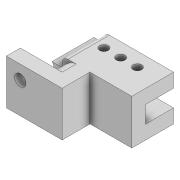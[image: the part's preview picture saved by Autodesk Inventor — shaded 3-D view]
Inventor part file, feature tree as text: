
AUTODESK INVENTOR PART (.ipt)
format: ipt  version: 2022 (Build 260153000, 153)  size: 222,208 bytes
history: native  units: mm
features: extrude x9, sketch x6, projected_geometry x6, pattern_linear x2, fillet x2, plane x1, mirror x1
ambient origin geometry x8: Origin, YZ Plane, XZ Plane, XY Plane, X Axis, Y Axis, Z Axis, Center Point
bodies: Solid1 (feature_tree)
feature tree (27):
  sketch  "Sketch2"  dims[d0=3.1mm d1=10.0mm]
  extrude  "Extrusion1"  Depth=10.0mm
  extrude  "Extrusion2"  Depth=30.0mm
  pattern_linear  "Rectangular Pattern1"  Count1=3 Spacing1=6.0mm
  pattern_linear  "Rectangular Pattern2"  Count1=2 Spacing1=11.1mm
  sketch  "Sketch3"  dims[d2=5.0mm d3=30.0mm]
  extrude  "Extrusion3"  Depth=2.0mm TaperAngle=0.0deg
  extrude  "Extrusion4"  Depth=10.0mm TaperAngle=0.0deg
  extrude  "Extrusion5"  Depth=2.0mm
  extrude  "Extrusion8"  Depth=5.0mm
  plane  "Work Plane2"
  mirror  "Mirror2"
  extrude  "Extrusion9"  Depth=5.0mm
  extrude  "Extrusion10"  Depth=5.0mm
  fillet  "Fillet1"  Radius=5.0mm
  fillet  "Fillet2"  Radius=5.0mm
  extrude  "Extrusion11"  Depth=5.0mm TaperAngle=0.0deg
  sketch  "Sketch5"  dims[d4=10.0mm]
  projected_geometry  "Projected Loop1"
  sketch  "Sketch6"  dims[d5=5.0mm d6=0.0mm]
  projected_geometry  "Projected Loop2"
  sketch  "Sketch7"  dims[d7=10.0mm d8=0.0mm d9=30.0mm d11=6.0mm d12=20.0mm d14=11.1mm]
  projected_geometry  "Projected Loop3"
  sketch  "Sketch8"  dims[d18=5.0mm d19=0.0mm d20=100.0mm d21=0.0mm d22=10.0mm d23=0.0mm d36=4.1mm d37=5.0mm d38=5.0mm d39=5.0mm d40=5.0mm d41=5.0mm d42=5.0mm d43=0.0mm d44=20.0mm d45=100.0mm d46=0.0mm d47=3.5mm d48=1.0mm d49=0.0mm d50=4.0mm d51=2.0mm d52=0.1mm d53=0.0mm]
  projected_geometry  "Projected Loop4"
  projected_geometry  "Project Cut Edges1"
  projected_geometry  "Project Cut Edges3"
